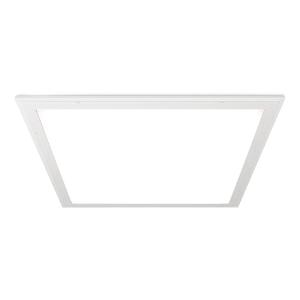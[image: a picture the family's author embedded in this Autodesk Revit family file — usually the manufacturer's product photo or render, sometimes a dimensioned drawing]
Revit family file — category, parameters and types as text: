
# Revit family: 3f_filippi_-_l_650_luce_diffusa_lgs_3f_filippi_-_21870_-_l_650_75w-940_dali_lgs_596x596
name_source: partatom
category: Lighting Fixtures
units: mm (PartAtom-declared; Revit-internal decimal feet)

## family parameters
Cut with Voids When Loaded = No
Host = Face
Light Source = No
Part Type = Normal
Room Calculation Point = No
Round Connector Dimension = Use Diameter
Shared = No

## types (1)
- 3F Filippi - L 650 Luce Diffusa LGS (1 x LED, 7545 lm, 81 W, 4000 K)
    Apparent Load = 81 VA
    Approval mark = ENEC
    CIE Flux Codes = 66 93 98 100 100
    Color Rendering = 90
    Color Temperature = 4000 K
    Control Gear = Electronic transformer
    Default Elevation = 1800 mm
    Description = ILLUMINOTECHNICAL
Luminous efficiency 100% (DLOR 100%, ULOR 0%).
Initial luminous flux of the luminaire 7545 lm.
Direct symmetric distribution.
Installation Interdistance Transv.D = 1.14 x hu - Long.D = 1.16 x hu.
Average luminance <3000 cd/m² for radial angles >65°.
Tabular UGR (CIE 117 - 4H-8H; S=0.25H; 70/50/20): RUG 19.2 - 19.1.
Beam angle: 85° - 85°.
Luminous efficacy 93 lm/W.
Lifetime (L93/B10): 30000 h. (tq+25°C)
Lifetime (L90/B10): 50000 h. (tq+25°C)
Lifetime (L85/B10): 80000 h. (tq+25°C)
Lifetime (L80/B10): 100000 h. (tq+25°C)
Sudden decreased luminous flux after 50000 hours: 0% (C0).
Photobiological safety in compliance with IEC/TR 62778: RG0 risk exempt, (IEC 62471).
In compliance with IEC/EN 62722-2-1 - IEC/EN 62717 standards.

SOURCE
Squared LED module 75W/940.
Source with special protection against aggressive chemically-volatile substances for standard LED technology.
Energy efficiency class (UE 2019/2020 - UE 2019/2015): E.
CIE 13.3 Colour rendering index: CRI >90 (R9 >50%).
IES TM-30 Fidelity Index: Rf = 92 Rg = 101.
CCT nominal colour temperature 4000 K.
Colour initial tolerance (MacAdam): SDCM 3.

MECHANICAL
Housing in galvannealed steel, painted in white epoxy-polyester.
Perimetral frame in white stainless steel.
LGS micro-prismatic flat diffuser in transparent methacrylate (PMMA), multi-lenticular exterior, anti-glare.
Anti-glare opal polycarbonate filter for brightness uniformity.
Luminaire with limited surface temperature. - D - (EN 60598-2-24)
Dimensions: 596x596 mm, height 90 mm. Weight 7 kg.
IP66 protection degree for exposed part, IP64 for recessed part.
Mechanical strength to impacts IK06 (1 joule).
Glow-wire test resistance 650°C.

ELECTRICAL
Halogen Free DALI-2 DATI (Parts 251, 252, 253), PUSH-DIM, electronic wiring 230V-50/60Hz, power factor 0.95 at full load, THD <25%, constant output current, SELV, class I, 1 driver, 1 DALI addresse.
Power of the luminaire 81 W.
CE - IEC 60598-1 - EN 60598-1.
SAFE FLICKER: PstLM=<1 and SVM=<0.4 (IEC TR 61547-1 and IEC TR 63158), to ensure a more comfortable and safe light.
Luminaire compliant with EN 60598-2-22 for power supply from a centralised emergency system CPSS (Central Power Supply System), not incorporated in the luminaire - high risk areas excluded. The default power and flux are 100% in AC and 15% in DC.
Ambient temperature from 0°C to +40°C.
Temperature class T6 max 85°C.
5-pole terminal block (L-N-PE-DA/DA) quick connection for line connection with connection capacity 2x2.5 mm² per poles.
Relative humidity UR: <85%.

INSTALLATION
Lay-in recessed fitting.
All accessories dedicated to this product are available on the Catalog and on our website www.3F-Filippi.com.

APPLICATIONS
Suitable product for food production plants (HACCP), IFS (Food Version 6), BRC (GSFS Food Version 7).
Environments: hospital premises, transit areas, laboratories, platform-roof, underpasses.
Environments: sterilized, aseptic.
In hospital environments, food industry or machines with parts in motion, with considerable sudden temperature changes, and in general in any environments requiring total protection against falling fragments, use luminaires with laminated glass only.
Tempered glass is not immune to falling fragments from harmless and caused by shocks or exceptionally derived from the tempering process.
Environments requiring a high level of protection and simplified cleaning.
Environments with exacting visual tasks, where diffused soft light for optimum visual comfort is required.

LIGHT MANAGEMENT
Recommended minimum setting: 10%.
The luminaire, equipped with (DALI-2 DATI) driver, can be controlled manually with 3F Easy Dim technology or automatically/manually with wired or wireless DALI/D2D control systems.
The D2D driver guarantees interoperability with other devices with the same certification by making the following information available:
Device Data (Part 251), Energy Report (Part 252), Diagnosis & Maintenance (Part 253).
In electrical systems without a regulation system (manual or automatic) and DALI bus, a suitable jumper must be made on the DA-DA terminals of the appliance.

WARNING
Luminaire designed for disposal/recycling at end-of-life.
Replaceable (LED only) light source by a professional. Replaceable control gear by a professional.
    Height = 0 mm  [stored 0 ft]
    Lamp = 1 x LED
    Lamp Light Flux = 7545 lm
    Lamp Power = 81 W
    Lamp count = 1
    Length = 596 mm
    Lifetime = 50000 h
    Luminous efficacy = 93 lm/W
    Manufacturer = 3F Filippi
    ModVariant = No
    Model = 3F Filippi - 21870 - L 650 75W-940 DALI LGS 596x596
    Mounting Place = Ceiling
    Mounting Type = Recessed
    Number of Poles = 1
    OnlyDefault = Yes
    Power Factor = 1
    Product Name = 3F Filippi - L 650 Luce Diffusa LGS
    Product group = recessed luminaire
    ProductGroupID = 4
    Protection Class = Protection class I
    Protection Degree = IP 64
    RLX_Detail_Level = 1
    RLX_Emergency_Light_Flux = 0 lm
    RLX_Emergency_Type = 0
    RLX_Emergency_Type_DB = No
    RlxData = <blob elided: 101193 chars, md5=8c2037a7>
    Socket = socket
    Standby Power = 0 W
    System Light Flux = 7545 lm
    System Power = 81 W
    Type Comments = Product without accessories
    Type Image = 3ffilippi_l_650_luce_diffusa_lgs.jpg
    URL = http://relux.com
    VarID = ---
    Voltage = 0 V
    Weight = 0.00 kg
    Width = 596 mm

note: [stored X ft] marks values corroborated as IEEE doubles in the binary element streams (Revit-internal decimal feet)

## geometry (parser evidence)
native form markers: Blend x4, Sweep x10
no freeform markers — native parametric forms only
